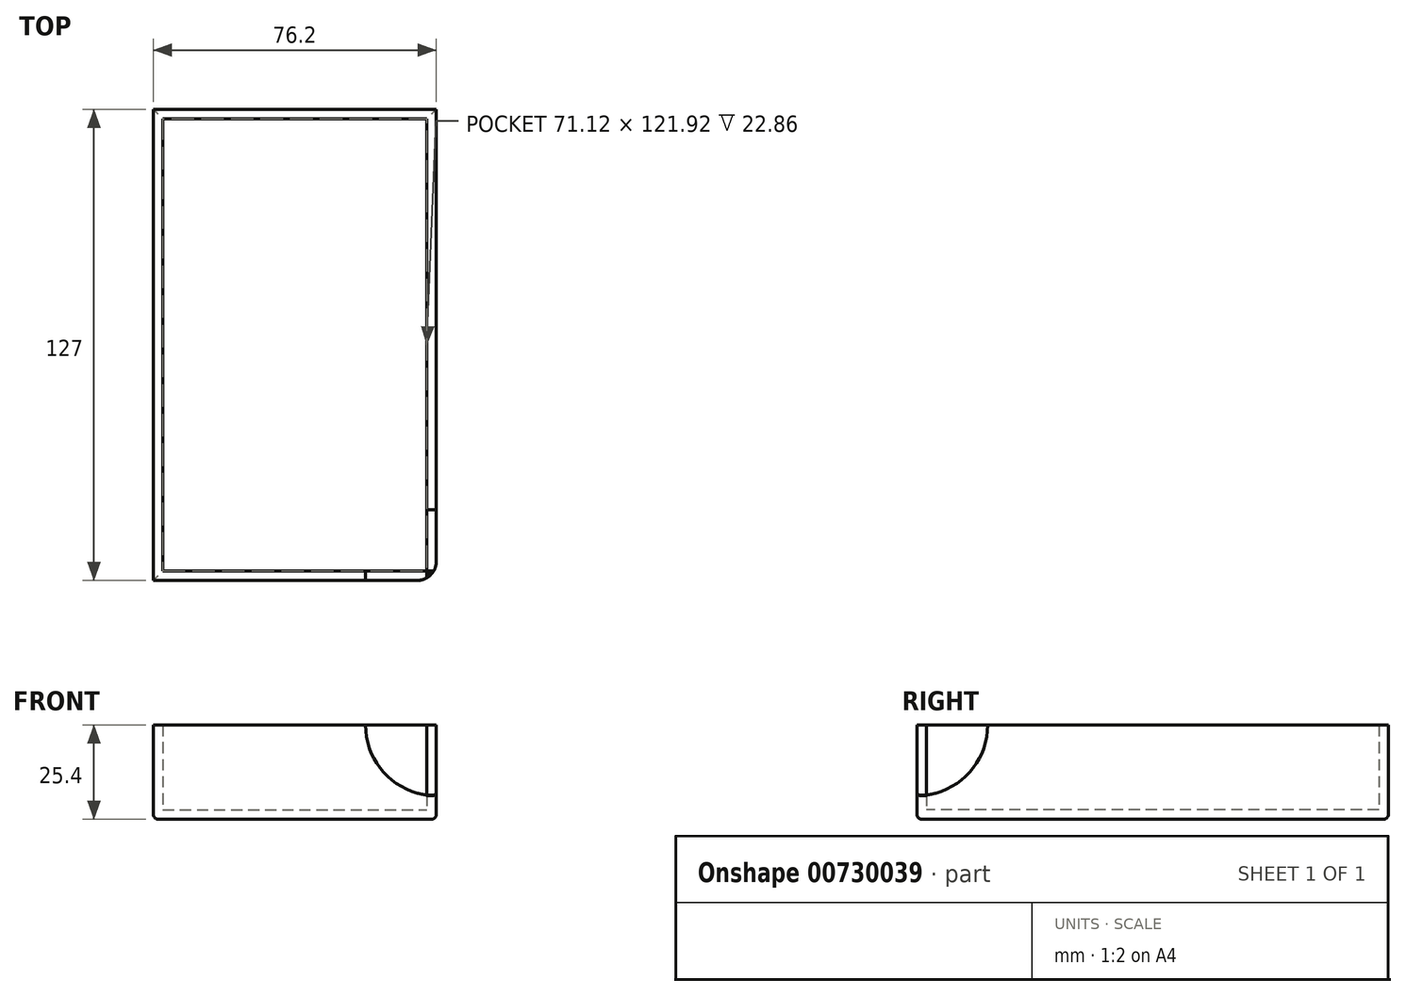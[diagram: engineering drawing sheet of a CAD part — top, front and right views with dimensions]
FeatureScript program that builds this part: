
annotation { "Feature Type Name" : "Feature", "Feature Type Description" : "" }
export const myFeature = defineFeature(function(context is Context, id is Id, definition is map)
    precondition{}
    {
        {
            var Q0;
            Q0=qCreatedBy(makeId("Top.planeOp"),FACE);
            var sketch = newSketch(context, id + "F0", { "sketchPlane" : qUnion([Q0])});
            skLineSegment(sketch, "E0.bottom", {"start": v(-38.1, 63.5) * mm, "end": v(38.1, 63.5) * mm});
            skLineSegment(sketch, "E0.top", {"start": v(-38.1, -63.5) * mm, "end": v(38.1, -63.5) * mm});
            skLineSegment(sketch, "E0.left", {"start": v(-38.1, 63.5) * mm, "end": v(-38.1, -63.5) * mm});
            skLineSegment(sketch, "E0.right", {"start": v(38.1, 63.5) * mm, "end": v(38.1, -63.5) * mm});
            skPoint(sketch, "E0.middle", {"position": v(0, 0) * mm});
            skLineSegment(sketch, "E1.0", {"start": v(-35.56, 60.96) * mm, "end": v(35.56, 60.96) * mm});
            skLineSegment(sketch, "E1.1", {"start": v(-35.56, 60.96) * mm, "end": v(-35.56, -60.96) * mm});
            skLineSegment(sketch, "E1.2", {"start": v(-35.56, -60.96) * mm, "end": v(35.56, -60.96) * mm});
            skLineSegment(sketch, "E1.3", {"start": v(35.56, 60.96) * mm, "end": v(35.56, -60.96) * mm});
            skSolve(sketch);
        }
        {
            var Q0;
            Q0 = qSketchRegion(id + "F0", true);
            extrude(context, id + "F1", {"entities" : qUnion([Q0]), "depth" : 25.4 * mm, "offsetDistance" : 25.4 * mm});
        }
        {
            var Q0;
            Q0=makeQuery(id+"F0.imprint","IMPRINT",FACE,{"disambiguationData":[TD([[makeQuery(id+"F0.imprint","IMPRINT",EDGE,{"derivedFrom":sQuery(id+"F0.wireOp",EDGE,"E1.0")}),-1.0]])]});
            extrude(context, id + "F2", {"entities" : qUnion([Q0]), "operationType" : NewBodyOperationType.ADD, "depth" : 2.54 * mm, "offsetDistance" : 25.4 * mm});
        }
        {
            var Q0;
            Q0=makeQuery(id+"F1.opExtrude","SWEPT_FACE",FACE,{"disambiguationData":[OSD([sQuery(id+"F0.wireOp",EDGE,"E0.right")])]});
            var sketch = newSketch(context, id + "F3", { "sketchPlane" : qUnion([Q0])});
            skArc(sketch, "E2", {"start": v(-63.5, 6.35) * mm, "mid": v(-50.03, 11.93) * mm, "end": v(-44.45, 25.4) * mm});
            skSolve(sketch);
        }
        {
            var Q0;
            Q0=makeQuery(id+"F1.opExtrude","SWEPT_FACE",FACE,{"disambiguationData":[OSD([sQuery(id+"F0.wireOp",EDGE,"E0.top")])]});
            var sketch = newSketch(context, id + "F4", { "sketchPlane" : qUnion([Q0])});
            skArc(sketch, "E3", {"start": v(19.05, 25.4) * mm, "mid": v(24.63, 11.93) * mm, "end": v(38.1, 6.35) * mm});
            skSolve(sketch);
        }
        {
            var Q0;
            {var subQ0=sQuery(id+"F3.wireOp",EDGE,"E2");Q0=makeQuery(id+"F3.imprint","IMPRINT",FACE,{"disambiguationData":[TD([[makeQuery(id+"F3.imprint","IMPRINT",EDGE,{"derivedFrom":subQ0}),1.0]])]});}
            extrude(context, id + "F5", {"entities" : qUnion([Q0]), "operationType" : NewBodyOperationType.REMOVE, "oppositeDirection" : true, "depth" : 2.54 * mm, "offsetDistance" : 25.4 * mm});
        }
        {
            var Q0;
            {var subQ0=sQuery(id+"F4.wireOp",EDGE,"E3");Q0=makeQuery(id+"F4.imprint","IMPRINT",FACE,{"disambiguationData":[TD([[makeQuery(id+"F4.imprint","IMPRINT",EDGE,{"derivedFrom":subQ0}),1.0]])]});}
            extrude(context, id + "F6", {"entities" : qUnion([Q0]), "operationType" : NewBodyOperationType.REMOVE, "oppositeDirection" : true, "depth" : 2.54 * mm, "offsetDistance" : 25.4 * mm});
        }
        {
            var Q0;
            Q0=makeQuery(id+"F1.opExtrude","SWEPT_EDGE",EDGE,{"disambiguationData":[OSD([sQuery(id+"F0.wireOp",EDGE,"E0.top"),sQuery(id+"F0.wireOp",EDGE,"E0.right")])]});
            var Q1;
            Q1=makeQuery(id+"F6.boolean.opBoolean","COPY",EDGE,{"derivedFrom":makeQuery(id+"F6.opExtrude","CAP_EDGE",EDGE,{"disambiguationData":[OSD([sQuery(id+"F4.wireOp",EDGE,"E3")])],"isStart":true})});
            var Q2;
            Q2=makeQuery(id+"F5.boolean.opBoolean","COPY",EDGE,{"derivedFrom":makeQuery(id+"F5.opExtrude","CAP_EDGE",EDGE,{"disambiguationData":[OSD([sQuery(id+"F3.wireOp",EDGE,"E2")])],"isStart":true})});
            fillet(context, id + "F7", {"entities" : qUnion([Q0, Q1, Q2]), "radius" : 5.08 * mm, "tangentPropagation" : true, "allowEdgeOverflow" : false});
        }
        {
            var Q0;
            {var subQ0=sQuery(id+"F0.wireOp",EDGE,"E1.3");var subQ1=sQuery(id+"F0.wireOp",EDGE,"E1.2");var subQ2=sQuery(id+"F0.wireOp",EDGE,"E1.1");var subQ3=sQuery(id+"F0.wireOp",EDGE,"E1.0");Q0=makeQuery(id+"F2.boolean.opBoolean","MERGE",FACE,{"derivedFrom":[makeQuery(id+"F1.opExtrude","CAP_FACE",FACE,{"disambiguationData":[OSD([sQuery(id+"F0.wireOp",EDGE,"E0.bottom"),sQuery(id+"F0.wireOp",EDGE,"E0.top"),sQuery(id+"F0.wireOp",EDGE,"E0.left"),sQuery(id+"F0.wireOp",EDGE,"E0.right"),subQ3,subQ2,subQ1,subQ0])],"isStart":true}),makeQuery(id+"F2.opExtrude","CAP_FACE",FACE,{"disambiguationData":[OSD([subQ3,subQ2,subQ1,subQ0])],"isStart":true})]});}
            fillet(context, id + "F8", {"entities" : qUnion([Q0]), "radius" : 1.27 * mm, "tangentPropagation" : true, "allowEdgeOverflow" : false});
        }
    });
